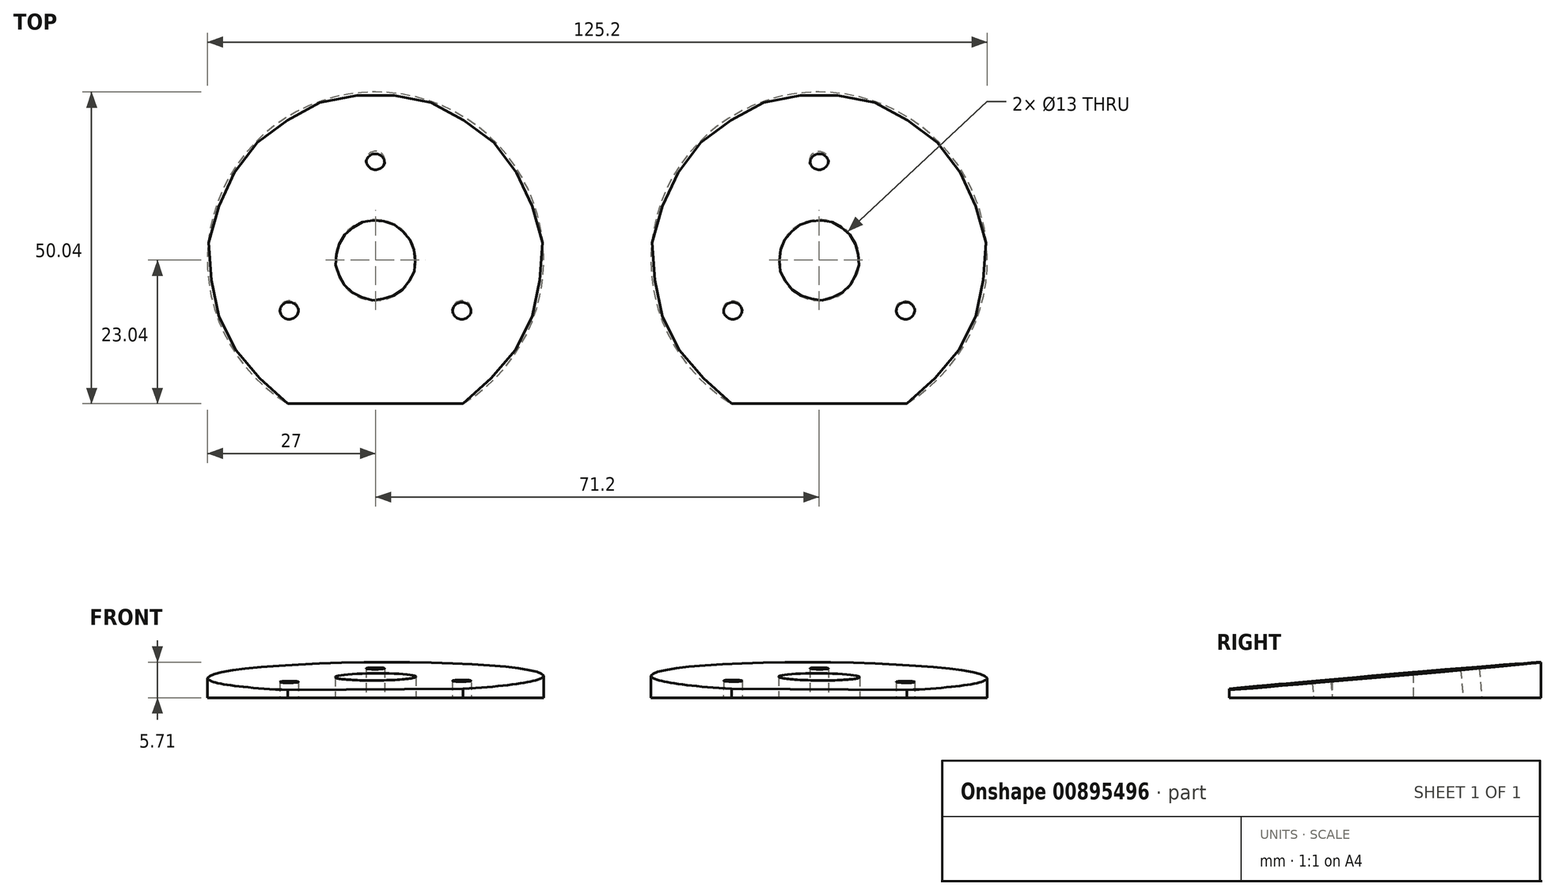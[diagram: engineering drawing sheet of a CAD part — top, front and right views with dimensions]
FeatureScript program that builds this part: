
annotation { "Feature Type Name" : "Feature", "Feature Type Description" : "" }
export const myFeature = defineFeature(function(context is Context, id is Id, definition is map)
    precondition{}
    {
        {
            var Q0;
            Q0=qCreatedBy(makeId("Top.planeOp"),FACE);
            var sketch = newSketch(context, id + "F0", { "sketchPlane" : qUnion([Q0])});
            skCircle(sketch, "E0", {"center": v(0, 0) * mm, "radius": 27 * mm});
            skLineSegment(sketch, "E1", {"start": v(0, 0) * mm, "end": v(0, -60) * mm, "construction": true});
            skLineSegment(sketch, "E2", {"start": v(0, 0) * mm, "end": v(-4.7, -59.82) * mm, "construction": true});
            skLineSegment(sketch, "E3", {"start": v(0, 0) * mm, "end": v(59.82, -4.7) * mm, "construction": true});
            skPoint(sketch, "E4.orphan", {"position": v(0, 11.85) * mm});
            skCircle(sketch, "E5", {"center": v(0, 0) * mm, "radius": 16 * mm, "construction": true});
            skCircle(sketch, "E6", {"center": v(0, 16) * mm, "radius": 1.5 * mm, "construction": true});
            skCircle(sketch, "E7.1.0", {"center": v(-13.86, -8) * mm, "radius": 1.5 * mm, "construction": true});
            skCircle(sketch, "E7.2.0", {"center": v(13.86, -8) * mm, "radius": 1.5 * mm, "construction": true});
            skLineSegment(sketch, "E8", {"start": v(-14.07, -23.04) * mm, "end": v(14.07, -23.04) * mm});
            skCircle(sketch, "E9", {"center": v(0, 0) * mm, "radius": 6.5 * mm});
            skSolve(sketch);
        }
        {
            var Q0;
            {var subQ0=sQuery(id+"F0.wireOp",EDGE,"E8");Q0=makeQuery(id+"F0.imprint","IMPRINT",FACE,{"disambiguationData":[TD([[makeQuery(id+"F0.imprint","IMPRINT",EDGE,{"derivedFrom":subQ0}),1.0]])]});}
            extrude(context, id + "F1", {"entities" : qUnion([Q0]), "depth" : 25 * mm, "offsetDistance" : 25 * mm});
        }
        {
            var Q0;
            Q0=qCreatedBy(makeId("Front.planeOp"),FACE);
            var sketch = newSketch(context, id + "F2", { "sketchPlane" : qUnion([Q0])});
            skLineSegment(sketch, "E10", {"start": v(0, 0) * mm, "end": v(0, 60) * mm, "construction": true});
            skSolve(sketch);
        }
        {
            var Q0;
            Q0=sQuery(id+"F0.wireOp",VERTEX,"E2.end");
            var Q1;
            Q1=sQuery(id+"F0.wireOp",VERTEX,"E1.start");
            var Q2;
            Q2=sQuery(id+"F2.wireOp",VERTEX,"E10.end");
            cPlane(context, id + "F3", {"entities" : qUnion([Q0, Q1, Q2]), "cplaneType" : CPlaneType.THREE_POINT, "offset" : 25 * mm, "width" : 150 * mm, "height" : 150 * mm});
        }
        {
            var Q0;
            Q0=qCreatedBy(id+"F3.planeOp",FACE);
            var sketch = newSketch(context, id + "F4", { "sketchPlane" : qUnion([Q0])});
            skLineSegment(sketch, "E11", {"start": v(-31.08, 31.4) * mm, "end": v(33.12, 31.4) * mm});
            skLineSegment(sketch, "E12", {"start": v(33.12, 31.4) * mm, "end": v(33.12, 0.45) * mm});
            skLineSegment(sketch, "E13", {"start": v(33.12, 0.45) * mm, "end": v(-31.08, 6.06) * mm});
            skLineSegment(sketch, "E14", {"start": v(-31.08, 6.06) * mm, "end": v(-31.08, 31.4) * mm});
            skSolve(sketch);
        }
        {
            var Q0;
            Q0 = qSketchRegion(id + "F4", true);
            extrude(context, id + "F5", {"entities" : qUnion([Q0]), "operationType" : NewBodyOperationType.REMOVE, "depth" : 100 * mm, "offsetDistance" : 25 * mm, "symmetric" : true});
        }
        {
            var Q0;
            Q0=makeQuery(id+"F5.boolean.opBoolean","COPY",FACE,{"derivedFrom":makeQuery(id+"F5.opExtrude","SWEPT_FACE",FACE,{"disambiguationData":[OSD([sQuery(id+"F4.wireOp",EDGE,"E13")])]})});
            var sketch = newSketch(context, id + "F6", { "sketchPlane" : qUnion([Q0])});
            skEllipse(sketch, "E15.0", {"center": v(0, 15.94) * mm, "majorRadius": 1.5 * mm, "minorRadius": 1.5 * mm, "majorAxis": v(1, -0.08)});
            skEllipse(sketch, "E15.1", {"center": v(-13.85, -7.97) * mm, "majorRadius": 1.5 * mm, "minorRadius": 1.5 * mm, "majorAxis": v(1, -0.08)});
            skEllipse(sketch, "E15.2", {"center": v(13.86, -7.97) * mm, "majorRadius": 1.5 * mm, "minorRadius": 1.5 * mm, "majorAxis": v(1, -0.08)});
            skSolve(sketch);
        }
        {
            var Q0;
            Q0 = qSketchRegion(id + "F6", true);
            extrude(context, id + "F7", {"entities" : qUnion([Q0]), "operationType" : NewBodyOperationType.REMOVE, "endBound" : BoundingType.THROUGH_ALL, "oppositeDirection" : true, "depth" : 25 * mm, "offsetDistance" : 25 * mm});
        }
        {
            var Q0;
            Q0=qCreatedBy(makeId("Right.planeOp"),FACE);
            cPlane(context, id + "F8", {"entities" : qUnion([Q0]), "cplaneType" : CPlaneType.OFFSET, "offset" : 35.6 * mm, "width" : 150 * mm, "height" : 150 * mm});
        }
        {
            var Q0;
            Q0=makeQuery(id+"F1.opExtrude","SWEPT_BODY",BODY,{"disambiguationData":[OSD([sQuery(id+"F0.wireOp",EDGE,"E0"),sQuery(id+"F0.wireOp",EDGE,"E8")])]});
            var Q1;
            Q1=qCreatedBy(id+"F8.planeOp",FACE);
            mirror(context, id + "F9", {"entities" : qUnion([Q0]), "mirrorPlane" : qUnion([Q1])});
        }
    });
